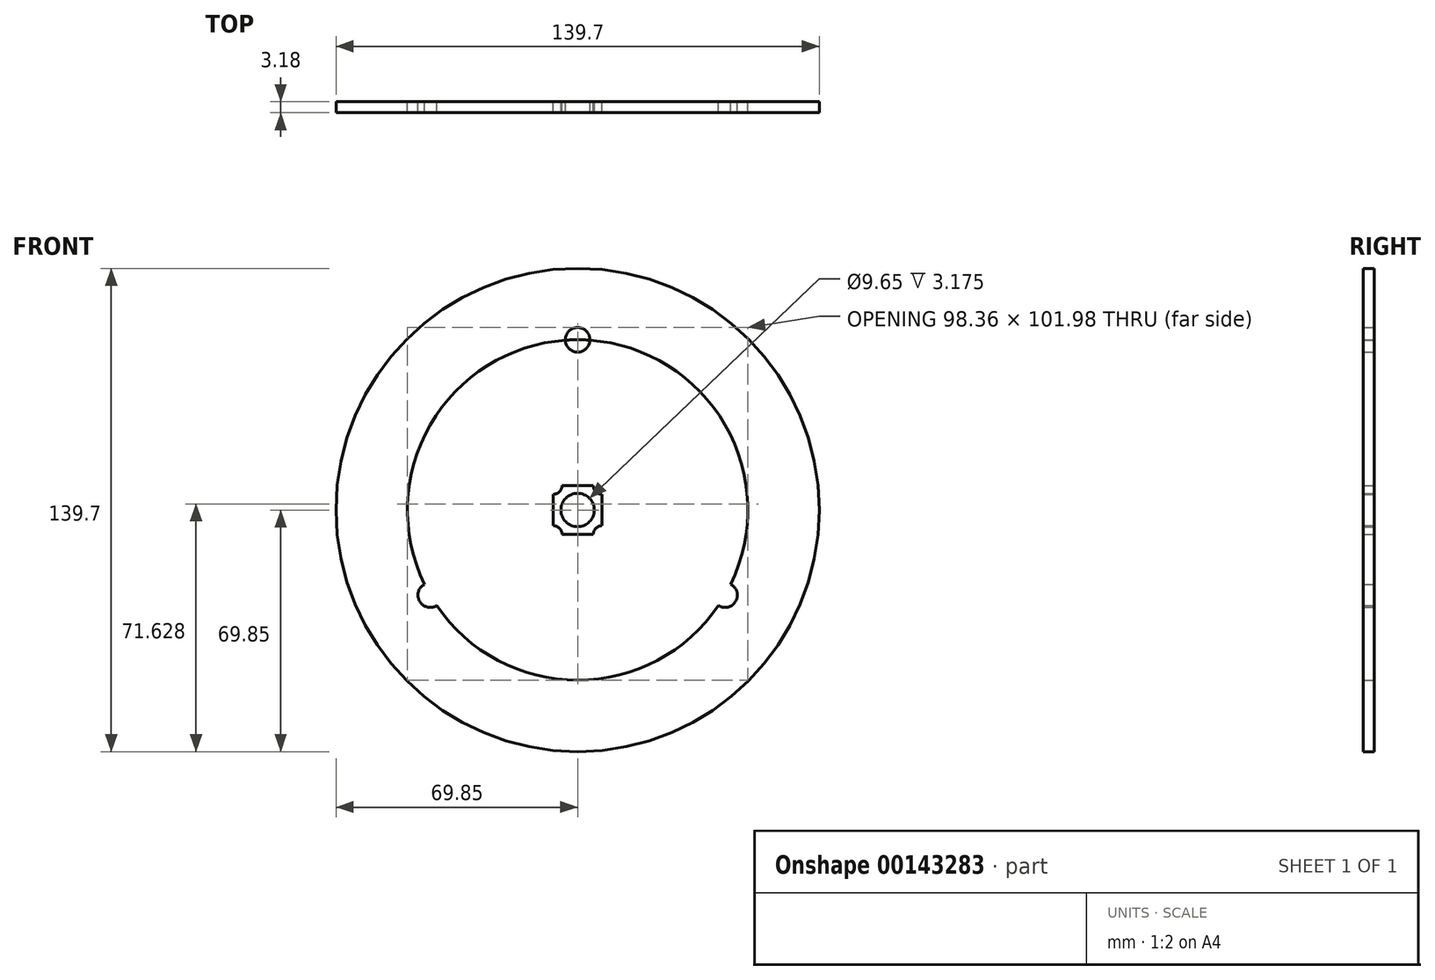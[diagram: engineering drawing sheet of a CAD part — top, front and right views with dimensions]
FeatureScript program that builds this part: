
annotation { "Feature Type Name" : "Feature", "Feature Type Description" : "" }
export const myFeature = defineFeature(function(context is Context, id is Id, definition is map)
    precondition{}
    {
        {
            var Q0;
            Q0=qCreatedBy(makeId("Front.planeOp"),FACE);
            var sketch = newSketch(context, id + "F0", { "sketchPlane" : qUnion([Q0])});
            skCircle(sketch, "E0", {"center": v(0, 0) * mm, "radius": 69.85 * mm});
            skCircle(sketch, "E1", {"center": v(0, 0) * mm, "radius": 49.21 * mm});
            skLineSegment(sketch, "E2.bottom", {"start": v(7.04, 7.04) * mm, "end": v(-7.04, 7.04) * mm});
            skLineSegment(sketch, "E2.top", {"start": v(7.04, -7.04) * mm, "end": v(-7.04, -7.04) * mm});
            skLineSegment(sketch, "E2.left", {"start": v(7.04, 7.04) * mm, "end": v(7.04, -7.04) * mm});
            skLineSegment(sketch, "E2.right", {"start": v(-7.04, 7.04) * mm, "end": v(-7.04, -7.04) * mm});
            skCircle(sketch, "E3", {"center": v(7.04, 7.04) * mm, "radius": 2.5 * mm});
            skCircle(sketch, "E4", {"center": v(7.04, -7.04) * mm, "radius": 2.5 * mm});
            skCircle(sketch, "E5", {"center": v(-7.04, -7.04) * mm, "radius": 2.5 * mm});
            skCircle(sketch, "E6", {"center": v(-7.04, 7.04) * mm, "radius": 2.5 * mm});
            skCircle(sketch, "E7", {"center": v(0, 49.21) * mm, "radius": 3.56 * mm});
            skCircle(sketch, "E8.1.0", {"center": v(-42.62, -24.6) * mm, "radius": 3.56 * mm});
            skCircle(sketch, "E8.2.0", {"center": v(42.62, -24.6) * mm, "radius": 3.56 * mm});
            skCircle(sketch, "E9", {"center": v(0, 0) * mm, "radius": 4.83 * mm});
            skSolve(sketch);
        }
        {
            var Q0;
            Q0 = qSketchRegion(id + "F0", true);
            var Q1;
            {var subQ11=sQuery(id+"F0.wireOp",EDGE,"E7");var subQ12=sQuery(id+"F0.wireOp",EDGE,"E1");var subQ13=makeQuery(id+"F0.imprint","INTERSECT",VERTEX,{"disambiguationData":[OD(0.0)],"derivedFrom":[subQ12,subQ11]});Q1=makeQuery(id+"F0.imprint","IMPRINT",FACE,{"disambiguationData":[TD([[makeQuery(id+"F0.imprint","IMPRINT",EDGE,{"disambiguationData":[TD([[subQ13,-1.0]])],"derivedFrom":subQ12}),1.0]])]});}
            var Q2;
            {var subQ5=sQuery(id+"F0.wireOp",EDGE,"E3");var subQ13=sQuery(id+"F0.wireOp",EDGE,"E2.bottom");var subQ14=makeQuery(id+"F0.imprint","INTERSECT",VERTEX,{"derivedFrom":[subQ13,subQ5]});Q2=makeQuery(id+"F0.imprint","IMPRINT",FACE,{"disambiguationData":[TD([[makeQuery(id+"F0.imprint","IMPRINT",EDGE,{"disambiguationData":[TD([[subQ14,-1.0]])],"derivedFrom":subQ13}),1.0]])]});}
            extrude(context, id + "F1", {"entities" : qUnion([Q0, Q1, Q2]), "depth" : 3.17 * mm});
        }
    });
